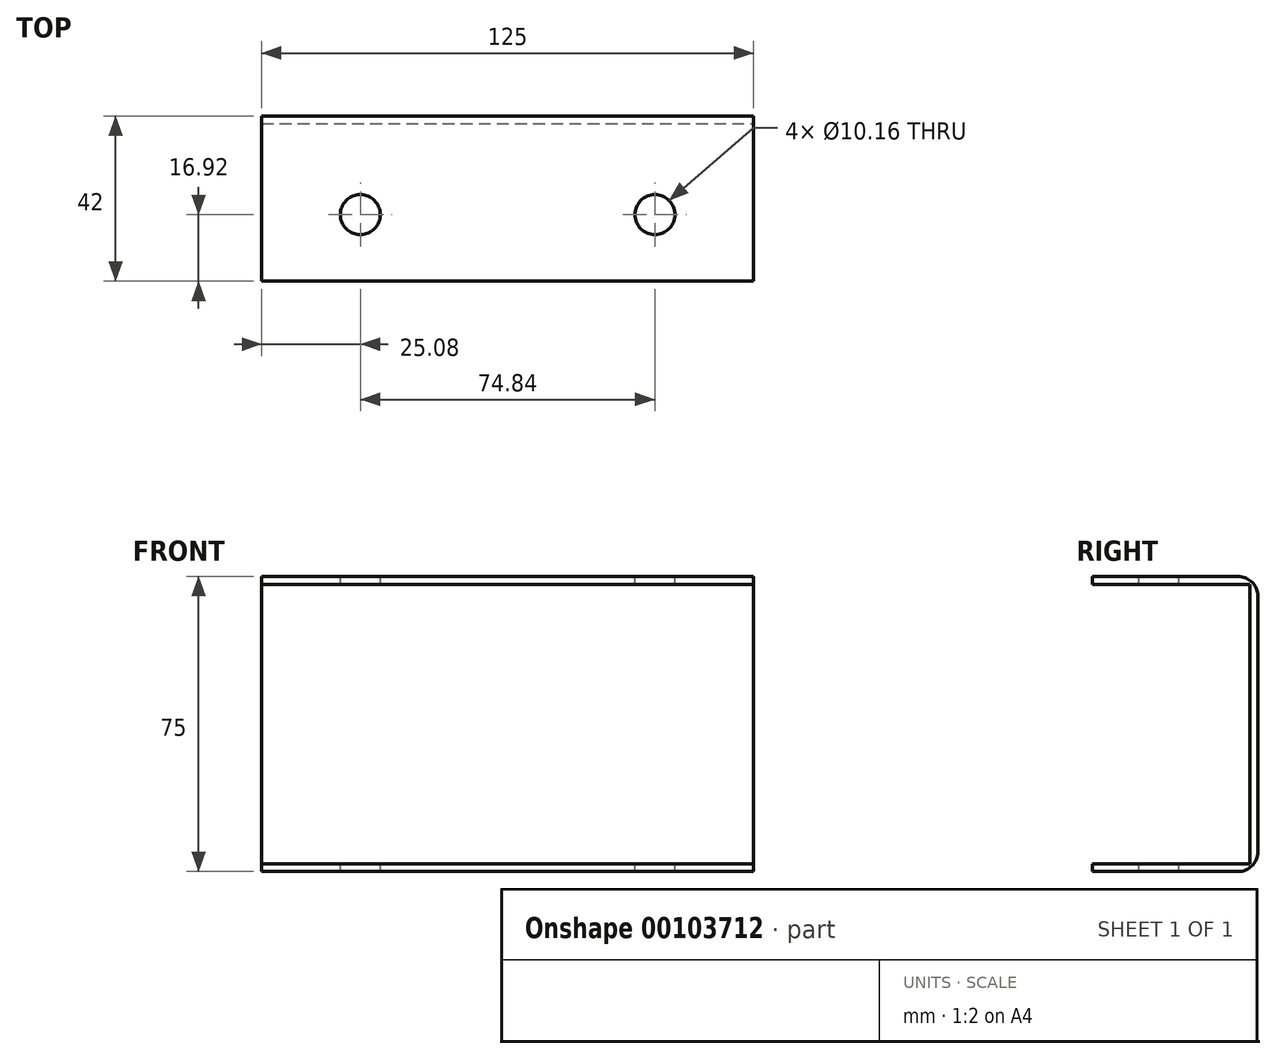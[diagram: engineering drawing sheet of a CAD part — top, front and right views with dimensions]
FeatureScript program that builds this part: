
annotation { "Feature Type Name" : "Feature", "Feature Type Description" : "" }
export const myFeature = defineFeature(function(context is Context, id is Id, definition is map)
    precondition{}
    {
        {
            var Q0;
            Q0=qCreatedBy(makeId("Front.planeOp"),FACE);
            var sketch = newSketch(context, id + "F0", { "sketchPlane" : qUnion([Q0])});
            skLineSegment(sketch, "E0.bottom", {"start": v(-62.5, 37.5) * mm, "end": v(62.5, 37.5) * mm});
            skLineSegment(sketch, "E0.top", {"start": v(-62.5, -37.5) * mm, "end": v(62.5, -37.5) * mm});
            skLineSegment(sketch, "E0.left", {"start": v(-62.5, 37.5) * mm, "end": v(-62.5, -37.5) * mm});
            skLineSegment(sketch, "E0.right", {"start": v(62.5, 37.5) * mm, "end": v(62.5, -37.5) * mm});
            skPoint(sketch, "E0.middle", {"position": v(0, 0) * mm});
            skSolve(sketch);
        }
        {
            var Q0;
            Q0=makeQuery(id+"F0.imprint","IMPRINT",FACE,{"disambiguationData":[TD([[makeQuery(id+"F0.imprint","IMPRINT",EDGE,{"derivedFrom":sQuery(id+"F0.wireOp",EDGE,"E0.bottom")}),-1.0]])]});
            extrude(context, id + "F1", {"entities" : qUnion([Q0]), "depth" : 2 * mm});
        }
        {
            var Q0;
            Q0=makeQuery(id+"F1.opExtrude","CAP_FACE",FACE,{"disambiguationData":[OSD([sQuery(id+"F0.wireOp",EDGE,"E0.bottom"),sQuery(id+"F0.wireOp",EDGE,"E0.top"),sQuery(id+"F0.wireOp",EDGE,"E0.left"),sQuery(id+"F0.wireOp",EDGE,"E0.right")])],"isStart":false});
            var sketch = newSketch(context, id + "F2", { "sketchPlane" : qUnion([Q0])});
            skLineSegment(sketch, "E1.bottom", {"start": v(-62.5, 37.5) * mm, "end": v(62.5, 37.5) * mm});
            skLineSegment(sketch, "E1.top", {"start": v(-62.5, 35.5) * mm, "end": v(62.5, 35.5) * mm});
            skLineSegment(sketch, "E1.left", {"start": v(-62.5, 37.5) * mm, "end": v(-62.5, 35.5) * mm});
            skLineSegment(sketch, "E1.right", {"start": v(62.5, 37.5) * mm, "end": v(62.5, 35.5) * mm});
            skLineSegment(sketch, "E2.bottom", {"start": v(-62.5, -37.5) * mm, "end": v(62.5, -37.5) * mm});
            skLineSegment(sketch, "E2.top", {"start": v(-62.5, -35.5) * mm, "end": v(62.5, -35.5) * mm});
            skLineSegment(sketch, "E2.left", {"start": v(-62.5, -37.5) * mm, "end": v(-62.5, -35.5) * mm});
            skLineSegment(sketch, "E2.right", {"start": v(62.5, -37.5) * mm, "end": v(62.5, -35.5) * mm});
            skSolve(sketch);
        }
        {
            var Q0;
            Q0=makeQuery(id+"F2.imprint","IMPRINT",FACE,{"disambiguationData":[TD([[makeQuery(id+"F2.imprint","IMPRINT",EDGE,{"derivedFrom":sQuery(id+"F2.wireOp",EDGE,"E2.bottom")}),1.0]])]});
            var Q1;
            Q1=makeQuery(id+"F2.imprint","IMPRINT",FACE,{"disambiguationData":[TD([[makeQuery(id+"F2.imprint","IMPRINT",EDGE,{"derivedFrom":sQuery(id+"F2.wireOp",EDGE,"E1.bottom")}),-1.0]])]});
            extrude(context, id + "F3", {"entities" : qUnion([Q0, Q1]), "operationType" : NewBodyOperationType.ADD, "depth" : 40 * mm});
        }
        {
            var Q0;
            Q0=makeQuery(id+"F1.opExtrude","CAP_EDGE",EDGE,{"disambiguationData":[OSD([sQuery(id+"F0.wireOp",EDGE,"E0.bottom")])],"isStart":true});
            var Q1;
            Q1=makeQuery(id+"F1.opExtrude","CAP_EDGE",EDGE,{"disambiguationData":[OSD([sQuery(id+"F0.wireOp",EDGE,"E0.top")])],"isStart":true});
            fillet(context, id + "F4", {"entities" : qUnion([Q0, Q1]), "radius" : 5 * mm, "tangentPropagation" : true, "allowEdgeOverflow" : false});
        }
        {
            var Q0;
            Q0=makeQuery(id+"F3.boolean.opBoolean","MERGE",FACE,{"derivedFrom":[makeQuery(id+"F1.opExtrude","SWEPT_FACE",FACE,{"disambiguationData":[OSD([sQuery(id+"F0.wireOp",EDGE,"E0.bottom")])]}),makeQuery(id+"F3.opExtrude","SWEPT_FACE",FACE,{"disambiguationData":[OSD([sQuery(id+"F2.wireOp",EDGE,"E1.bottom")])]})]});
            var sketch = newSketch(context, id + "F5", { "sketchPlane" : qUnion([Q0])});
            skCircle(sketch, "E3", {"center": v(-37.42, -25.08) * mm, "radius": 5.08 * mm});
            skCircle(sketch, "E4", {"center": v(37.42, -25.08) * mm, "radius": 5.08 * mm});
            skSolve(sketch);
        }
        {
            var Q0;
            Q0=makeQuery(id+"F5.imprint","IMPRINT",FACE,{"disambiguationData":[TD([[makeQuery(id+"F5.imprint","IMPRINT",EDGE,{"derivedFrom":sQuery(id+"F5.wireOp",EDGE,"E4")}),1.0]])]});
            var Q1;
            Q1=makeQuery(id+"F5.imprint","IMPRINT",FACE,{"disambiguationData":[TD([[makeQuery(id+"F5.imprint","IMPRINT",EDGE,{"derivedFrom":sQuery(id+"F5.wireOp",EDGE,"E3")}),1.0]])]});
            extrude(context, id + "F6", {"entities" : qUnion([Q0, Q1]), "operationType" : NewBodyOperationType.REMOVE, "oppositeDirection" : true, "depth" : 100 * mm});
        }
    });
